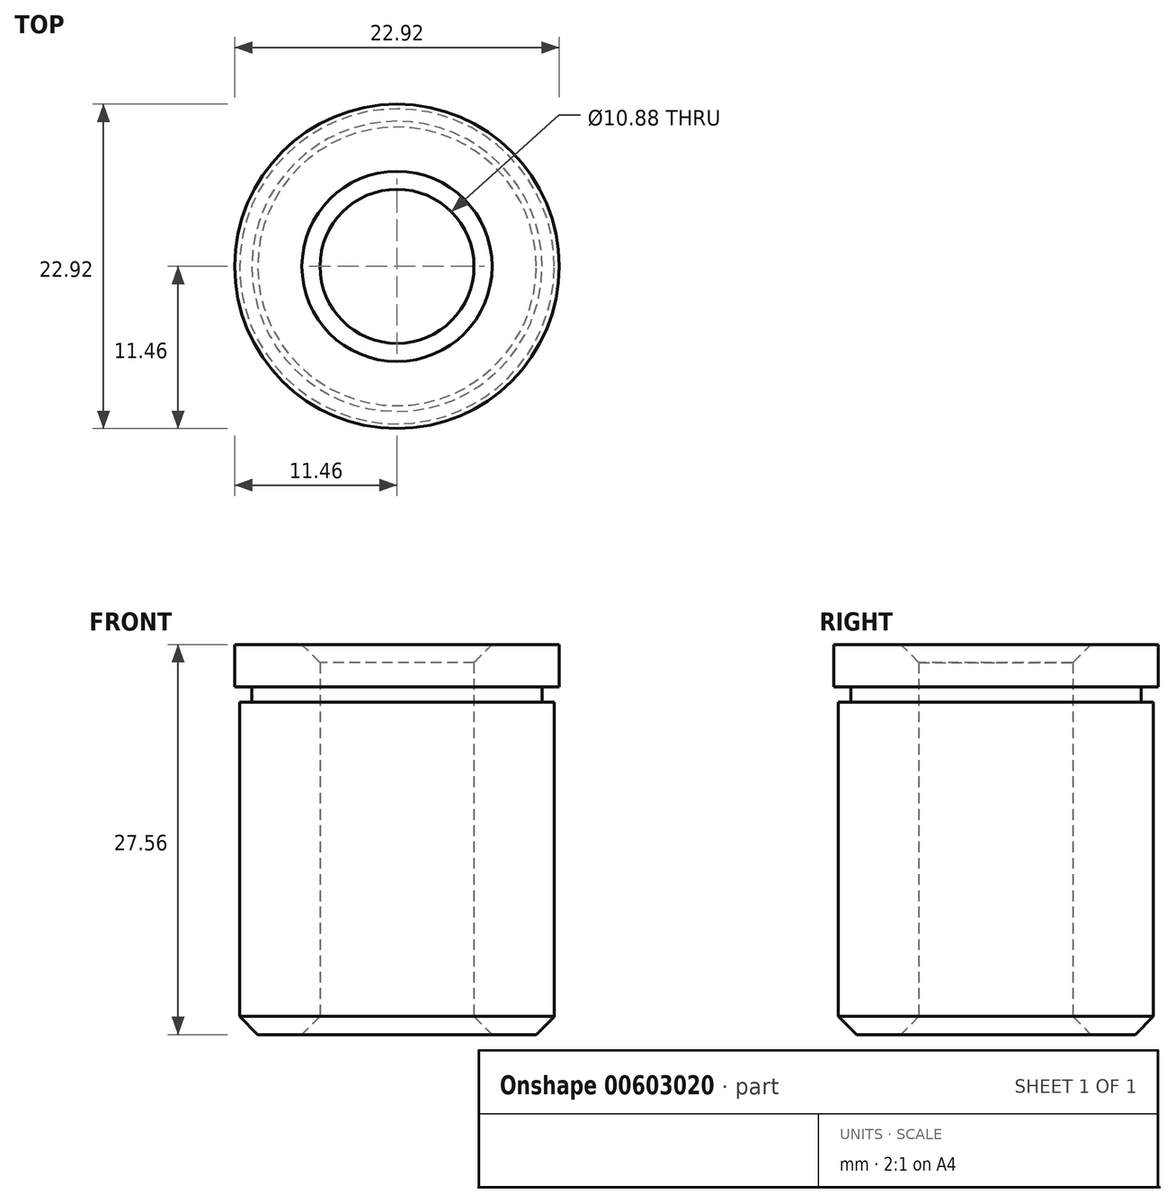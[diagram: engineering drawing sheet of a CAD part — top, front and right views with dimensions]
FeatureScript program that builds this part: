
annotation { "Feature Type Name" : "Feature", "Feature Type Description" : "" }
export const myFeature = defineFeature(function(context is Context, id is Id, definition is map)
    precondition{}
    {
        {
            var Q0;
            Q0=qCreatedBy(makeId("Top.planeOp"),FACE);
            var sketch = newSketch(context, id + "F0", { "sketchPlane" : qUnion([Q0])});
            skCircle(sketch, "E0", {"center": v(0, 0) * mm, "radius": 11.12 * mm});
            skCircle(sketch, "E1", {"center": v(0, 0) * mm, "radius": 5.44 * mm});
            skSolve(sketch);
        }
        {
            var Q0;
            Q0 = qSketchRegion(id + "F0", true);
            extrude(context, id + "F1", {"entities" : qUnion([Q0]), "depth" : 23.48 * mm, "offsetDistance" : 25 * mm});
        }
        {
            var Q0;
            Q0=qCreatedBy(makeId("Top.planeOp"),FACE);
            cPlane(context, id + "F2", {"entities" : qUnion([Q0]), "cplaneType" : CPlaneType.OFFSET, "offset" : 23.48 * mm, "width" : 150 * mm, "height" : 150 * mm});
        }
        {
            var Q0;
            Q0=qCreatedBy(id+"F2.planeOp",FACE);
            var sketch = newSketch(context, id + "F3", { "sketchPlane" : qUnion([Q0])});
            skCircle(sketch, "E2", {"center": v(0, 0) * mm, "radius": 5.44 * mm});
            skCircle(sketch, "E3", {"center": v(0, 0) * mm, "radius": 10.25 * mm});
            skSolve(sketch);
        }
        {
            var Q0;
            Q0 = qSketchRegion(id + "F3", true);
            extrude(context, id + "F4", {"entities" : qUnion([Q0]), "operationType" : NewBodyOperationType.ADD, "depth" : 1.08 * mm, "offsetDistance" : 25 * mm});
        }
        {
            var Q0;
            Q0=qCreatedBy(id+"F2.planeOp",FACE);
            cPlane(context, id + "F5", {"entities" : qUnion([Q0]), "cplaneType" : CPlaneType.OFFSET, "offset" : 1.08 * mm, "width" : 150 * mm, "height" : 150 * mm});
        }
        {
            var Q0;
            Q0=qCreatedBy(id+"F5.planeOp",FACE);
            var sketch = newSketch(context, id + "F6", { "sketchPlane" : qUnion([Q0])});
            skCircle(sketch, "E4", {"center": v(0, 0) * mm, "radius": 11.46 * mm});
            skCircle(sketch, "E5", {"center": v(0, 0) * mm, "radius": 5.44 * mm});
            skSolve(sketch);
        }
        {
            var Q0;
            Q0 = qSketchRegion(id + "F6", true);
            extrude(context, id + "F7", {"entities" : qUnion([Q0]), "operationType" : NewBodyOperationType.ADD, "depth" : 3 * mm, "offsetDistance" : 25 * mm});
        }
        {
            var Q0;
            Q0=makeQuery(id+"F1.opExtrude","CAP_EDGE",EDGE,{"disambiguationData":[OSD([sQuery(id+"F0.wireOp",EDGE,"E0")])],"isStart":true});
            chamfer(context, id + "F8", {"entities" : qUnion([Q0]), "width" : 1.28 * mm, "tangentPropagation" : true});
        }
        {
            var Q0;
            Q0=makeQuery(id+"F1.opExtrude","CAP_EDGE",EDGE,{"disambiguationData":[OSD([sQuery(id+"F0.wireOp",EDGE,"E1")])],"isStart":true});
            chamfer(context, id + "F9", {"entities" : qUnion([Q0]), "width" : 1.28 * mm, "tangentPropagation" : true});
        }
        {
            var Q0;
            Q0=makeQuery(id+"F7.opExtrude","CAP_EDGE",EDGE,{"disambiguationData":[OSD([sQuery(id+"F6.wireOp",EDGE,"E5")])],"isStart":false});
            chamfer(context, id + "F10", {"entities" : qUnion([Q0]), "width" : 1.28 * mm, "tangentPropagation" : true});
        }
    });
